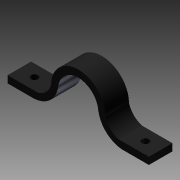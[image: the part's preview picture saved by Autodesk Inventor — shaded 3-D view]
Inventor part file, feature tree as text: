
AUTODESK INVENTOR PART (.ipt)
format: ipt  version: 2012 (Build 160160000, 160)  size: 112,128 bytes
history: native  units: mm
features: sketch x4, hole x2, extrude x1
ambient origin geometry x8: Origin, YZ Plane, XZ Plane, XY Plane, X Axis, Y Axis, Z Axis, Center Point
bodies: Solid1 (feature_tree)
feature tree (7):
  extrude  "Extrusion1"  Depth=3.0mm
  hole  "Hole1"  [1 undecoded]
  hole  "Hole2"  [1 undecoded]
  sketch  "Sketch4"  dims[d9=10.0mm d10=0.0mm d11=3.0mm d12=3.0mm d13=6.0mm d14=4.0mm d15=2.0mm d16=90.0deg d17=8.0mm d18=20.594885mm d19=3.0mm d20=3.0mm d21=6.0mm d22=4.0mm d23=2.0mm d24=90.0deg d25=8.0mm d26=20.594885mm]
  sketch  "Sketch1"  dims[d0=17.1mm d3=3.0mm]
  sketch  "Sketch2"  dims[d4=3.0mm d6=45.0deg]
  sketch  "Sketch3"  dims[d7=8.0mm d8=11.0mm]
note: 2 required parameter values undecoded (feature->parameter linkage not recoverable at this tier; creation-order binding heuristic only, values carry confidence <= 0.55)
